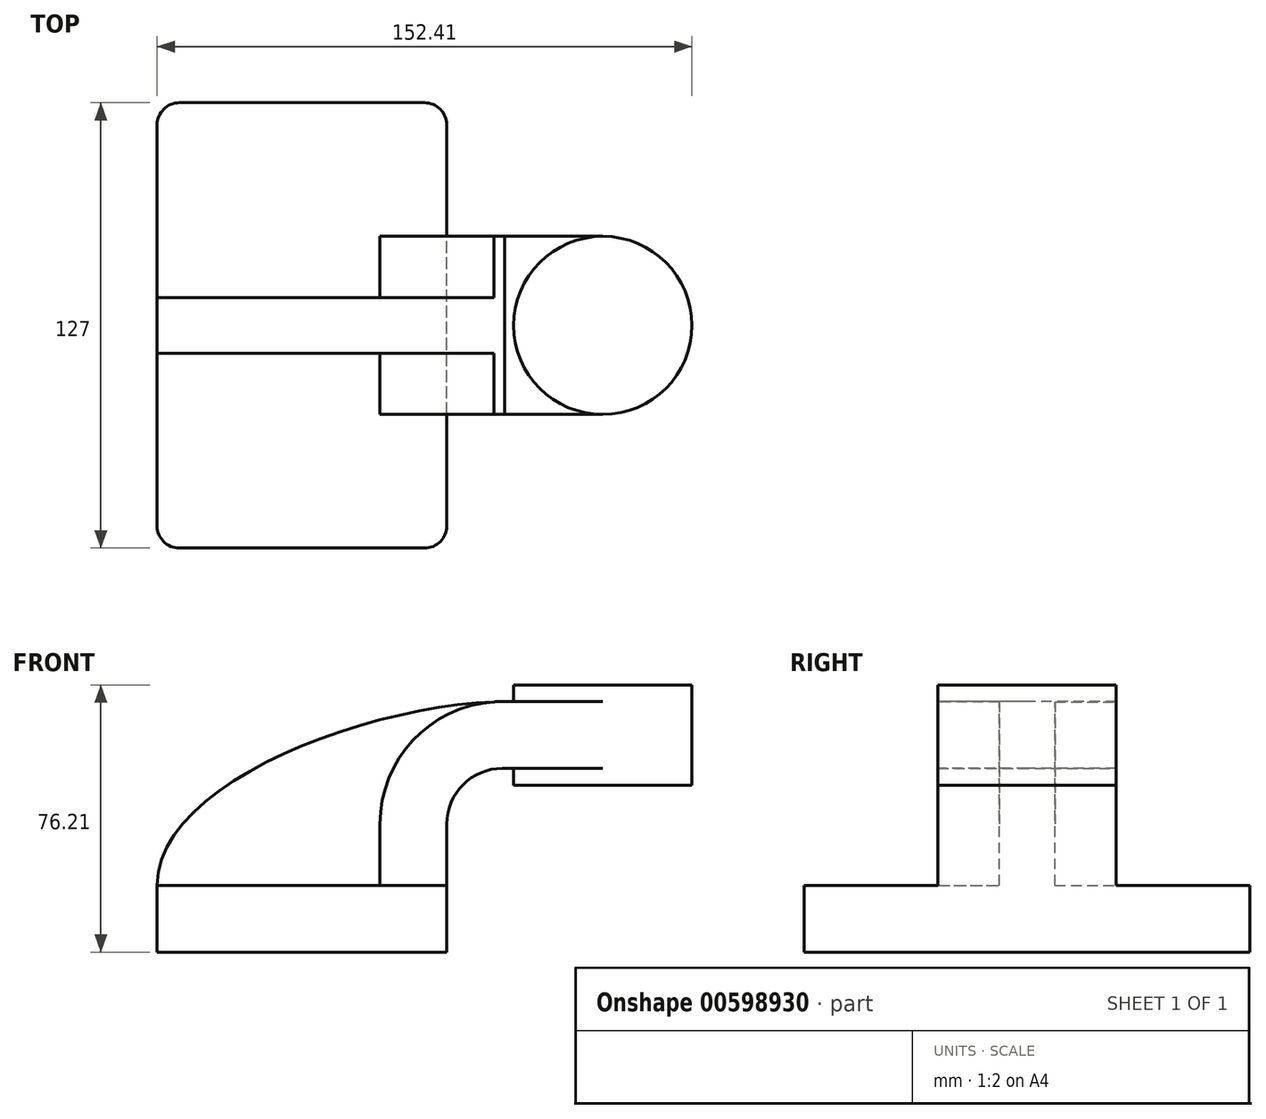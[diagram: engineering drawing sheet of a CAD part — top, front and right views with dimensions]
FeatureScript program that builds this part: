
annotation { "Feature Type Name" : "Feature", "Feature Type Description" : "" }
export const myFeature = defineFeature(function(context is Context, id is Id, definition is map)
    precondition{}
    {
        {
            var Q0;
            Q0=qCreatedBy(makeId("Front.planeOp"),FACE);
            var sketch = newSketch(context, id + "F0", { "sketchPlane" : qUnion([Q0])});
            skLineSegment(sketch, "E0.bottom", {"start": v(41.28, 9.53) * mm, "end": v(-41.28, 9.52) * mm});
            skLineSegment(sketch, "E0.top", {"start": v(41.28, -9.52) * mm, "end": v(-41.28, -9.53) * mm});
            skLineSegment(sketch, "E0.left", {"start": v(41.28, 9.53) * mm, "end": v(41.28, -9.53) * mm});
            skLineSegment(sketch, "E0.right", {"start": v(-41.28, 9.52) * mm, "end": v(-41.28, -9.53) * mm});
            skPoint(sketch, "E0.middle", {"position": v(0, 0) * mm});
            skLineSegment(sketch, "E1.bottom", {"start": v(111.12, 66.67) * mm, "end": v(60.33, 66.67) * mm});
            skLineSegment(sketch, "E1.top", {"start": v(111.12, 38.1) * mm, "end": v(60.33, 38.1) * mm});
            skLineSegment(sketch, "E1.left", {"start": v(111.12, 66.68) * mm, "end": v(111.12, 38.1) * mm});
            skLineSegment(sketch, "E1.right", {"start": v(60.32, 66.68) * mm, "end": v(60.33, 38.1) * mm});
            skPoint(sketch, "E1.middle", {"position": v(85.72, 52.39) * mm});
            skLineSegment(sketch, "E2", {"start": v(41.28, 9.53) * mm, "end": v(41.28, 27) * mm});
            skArc(sketch, "E3", {"start": v(41.27, 27) * mm, "mid": v(45.92, 38.23) * mm, "end": v(57.15, 42.88) * mm});
            skLineSegment(sketch, "E4", {"start": v(57.15, 42.88) * mm, "end": v(85.72, 42.88) * mm});
            skPoint(sketch, "E4.endSnap0", {"position": v(85.72, 38.1) * mm});
            skLineSegment(sketch, "E5.0", {"start": v(57.15, 61.93) * mm, "end": v(85.72, 61.93) * mm});
            skArc(sketch, "E5.1", {"start": v(22.23, 27) * mm, "mid": v(32.45, 51.7) * mm, "end": v(57.15, 61.93) * mm});
            skLineSegment(sketch, "E5.2", {"start": v(22.23, 9.53) * mm, "end": v(22.23, 27) * mm});
            skLineSegment(sketch, "E6", {"start": v(85.72, 38.1) * mm, "end": v(85.72, 66.67) * mm});
            skFitSpline(sketch, "E7", {"points": [v(-41.28, 9.52) * mm, v(60.33, 61.93) * mm], "startDerivative": vector(-0.04, 90.1) * mm, "endDerivative": vector(114.54, -1.54) * mm});
            skSolve(sketch);
        }
        {
            var Q0;
            Q0=makeQuery(id+"F0.imprint","IMPRINT",FACE,{"disambiguationData":[TD([[makeQuery(id+"F0.imprint","IMPRINT",EDGE,{"derivedFrom":sQuery(id+"F0.wireOp",EDGE,"E0.top")}),-1.0]])]});
            extrude(context, id + "F1", {"entities" : qUnion([Q0]), "endBound" : BoundingType.SYMMETRIC, "depth" : 127 * mm, "offsetDistance" : 25.4 * mm});
        }
        {
            var Q0;
            {var subQ1=sQuery(id+"F0.wireOp",EDGE,"E2");Q0=makeQuery(id+"F0.imprint","IMPRINT",FACE,{"disambiguationData":[TD([[makeQuery(id+"F0.imprint","IMPRINT",EDGE,{"derivedFrom":subQ1}),1.0]])]});}
            var Q1;
            {var subQ3=sQuery(id+"F0.wireOp",EDGE,"E4");var subQ5=sQuery(id+"F0.wireOp",EDGE,"E6");var subQ6=makeQuery(id+"F0.imprint","INTERSECT",VERTEX,{"derivedFrom":[subQ3,subQ5]});Q1=makeQuery(id+"F0.imprint","IMPRINT",FACE,{"disambiguationData":[TD([[makeQuery(id+"F0.imprint","IMPRINT",EDGE,{"disambiguationData":[TD([[subQ6,1.0]])],"derivedFrom":subQ3}),1.0]])]});}
            extrude(context, id + "F2", {"entities" : qUnion([Q0, Q1]), "operationType" : NewBodyOperationType.ADD, "endBound" : BoundingType.SYMMETRIC, "depth" : 50.8 * mm, "offsetDistance" : 25.4 * mm});
        }
        {
            var Q0;
            {var subQ3=sQuery(id+"F0.wireOp",EDGE,"E5.2");Q0=makeQuery(id+"F0.imprint","IMPRINT",FACE,{"disambiguationData":[TD([[makeQuery(id+"F0.imprint","IMPRINT",EDGE,{"derivedFrom":subQ3}),1.0]])]});}
            extrude(context, id + "F3", {"entities" : qUnion([Q0]), "operationType" : NewBodyOperationType.ADD, "endBound" : BoundingType.SYMMETRIC, "depth" : 15.88 * mm, "offsetDistance" : 25.4 * mm});
        }
        {
            var Q0;
            {var subQ4=sQuery(id+"F0.wireOp",EDGE,"E1.left");Q0=makeQuery(id+"F0.imprint","IMPRINT",FACE,{"disambiguationData":[TD([[makeQuery(id+"F0.imprint","IMPRINT",EDGE,{"derivedFrom":subQ4}),-1.0]])]});}
            var Q1;
            Q1=sQuery(id+"F0.wireOp",EDGE,"E6");
            revolve(context, id + "F4", {"operationType" : NewBodyOperationType.ADD, "entities" : qUnion([Q0]), "axis" : qUnion([Q1]), "revolveType" : RevolveType.FULL});
        }
        {
            var Q0;
            Q0=makeQuery(id+"F1.opExtrude","CAP_EDGE",EDGE,{"disambiguationData":[OSD([sQuery(id+"F0.wireOp",EDGE,"E0.left")])],"isStart":false});
            var Q1;
            Q1=makeQuery(id+"F1.opExtrude","CAP_EDGE",EDGE,{"disambiguationData":[OSD([sQuery(id+"F0.wireOp",EDGE,"E0.right")])],"isStart":false});
            var Q2;
            Q2=makeQuery(id+"F1.opExtrude","CAP_EDGE",EDGE,{"disambiguationData":[OSD([sQuery(id+"F0.wireOp",EDGE,"E0.left")])],"isStart":true});
            var Q3;
            Q3=makeQuery(id+"F1.opExtrude","CAP_EDGE",EDGE,{"disambiguationData":[OSD([sQuery(id+"F0.wireOp",EDGE,"E0.right")])],"isStart":true});
            fillet(context, id + "F5", {"entities" : qUnion([Q0, Q1, Q2, Q3]), "radius" : 6.35 * mm, "tangentPropagation" : true, "allowEdgeOverflow" : false});
        }
    });
